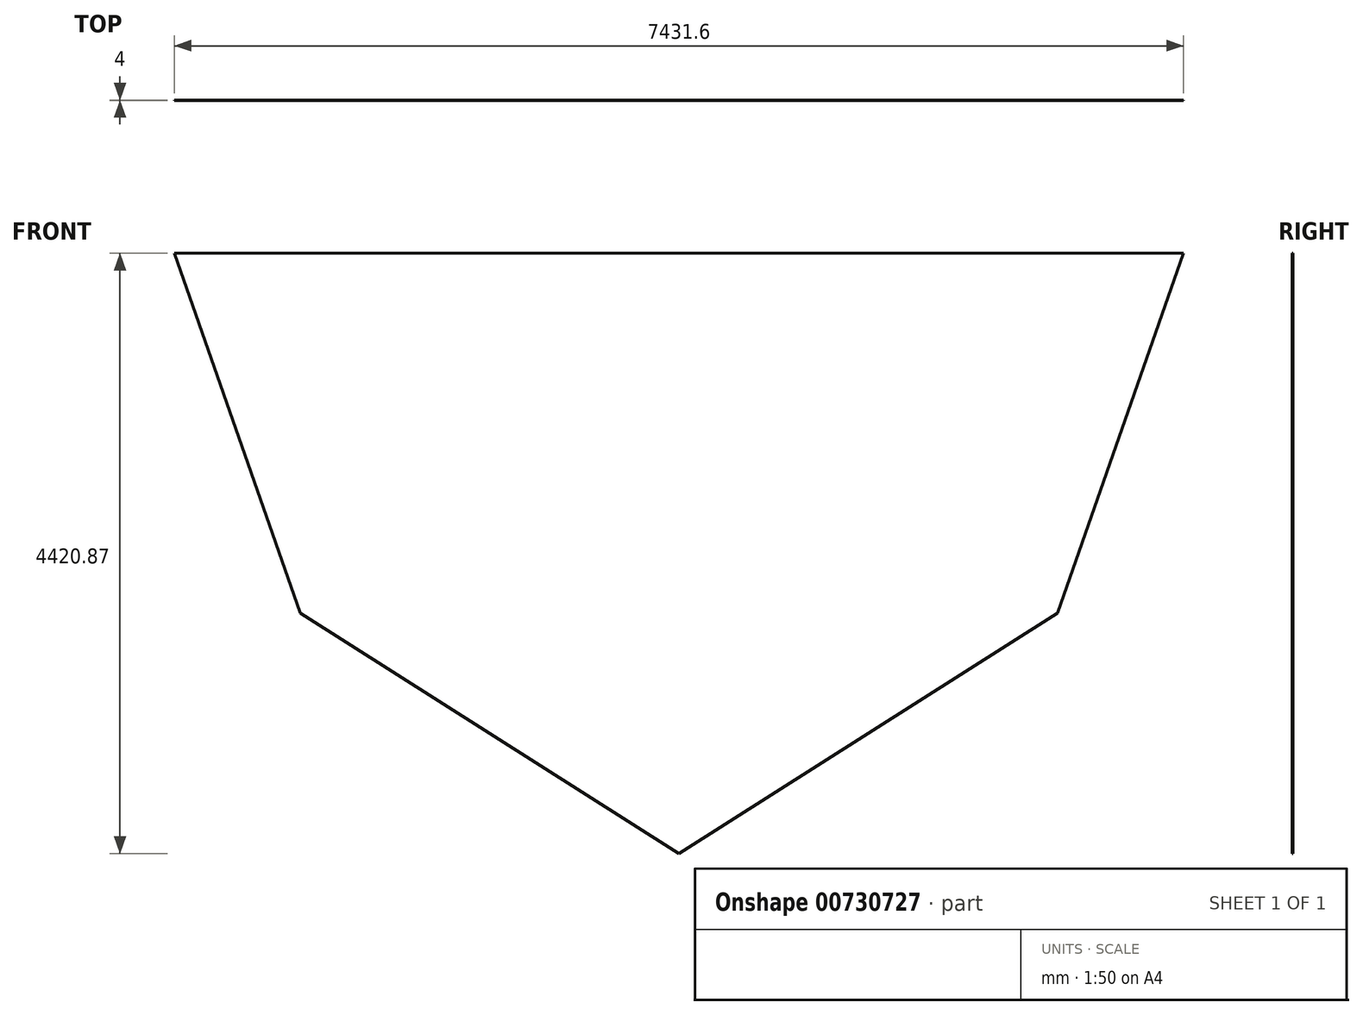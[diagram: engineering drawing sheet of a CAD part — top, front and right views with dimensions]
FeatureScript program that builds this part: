
annotation { "Feature Type Name" : "Feature", "Feature Type Description" : "" }
export const myFeature = defineFeature(function(context is Context, id is Id, definition is map)
    precondition{}
    {
        {
            var Q0;
            Q0=qCreatedBy(makeId("Front.planeOp"),FACE);
            var sketch = newSketch(context, id + "F0", { "sketchPlane" : qUnion([Q0])});
            skLineSegment(sketch, "E0", {"start": v(-3715.8, 2210.44) * mm, "end": v(-0.01, 2210.44) * mm});
            skLineSegment(sketch, "E1", {"start": v(-0.01, 2210.44) * mm, "end": v(-0.01, 2083.43) * mm});
            skLineSegment(sketch, "E2", {"start": v(-0.01, 2083.43) * mm, "end": v(-0.01, 2210.44) * mm});
            skLineSegment(sketch, "E3", {"start": v(-0.01, 2210.44) * mm, "end": v(3715.8, 2210.44) * mm});
            skLineSegment(sketch, "E4", {"start": v(3715.8, 2210.44) * mm, "end": v(2788.35, -440.61) * mm});
            skLineSegment(sketch, "E5", {"start": v(2788.35, -440.61) * mm, "end": v(-0.01, -2210.44) * mm});
            skLineSegment(sketch, "E6", {"start": v(-0.01, -2210.43) * mm, "end": v(-2788.37, -440.61) * mm});
            skLineSegment(sketch, "E7", {"start": v(-2788.37, -440.61) * mm, "end": v(-3715.8, 2210.44) * mm});
            skSolve(sketch);
        }
        {
            var Q0;
            Q0 = qSketchRegion(id + "F0", true);
            extrude(context, id + "F1", {"entities" : qUnion([Q0]), "depth" : 4 * mm, "offsetDistance" : 25 * mm});
        }
    });
